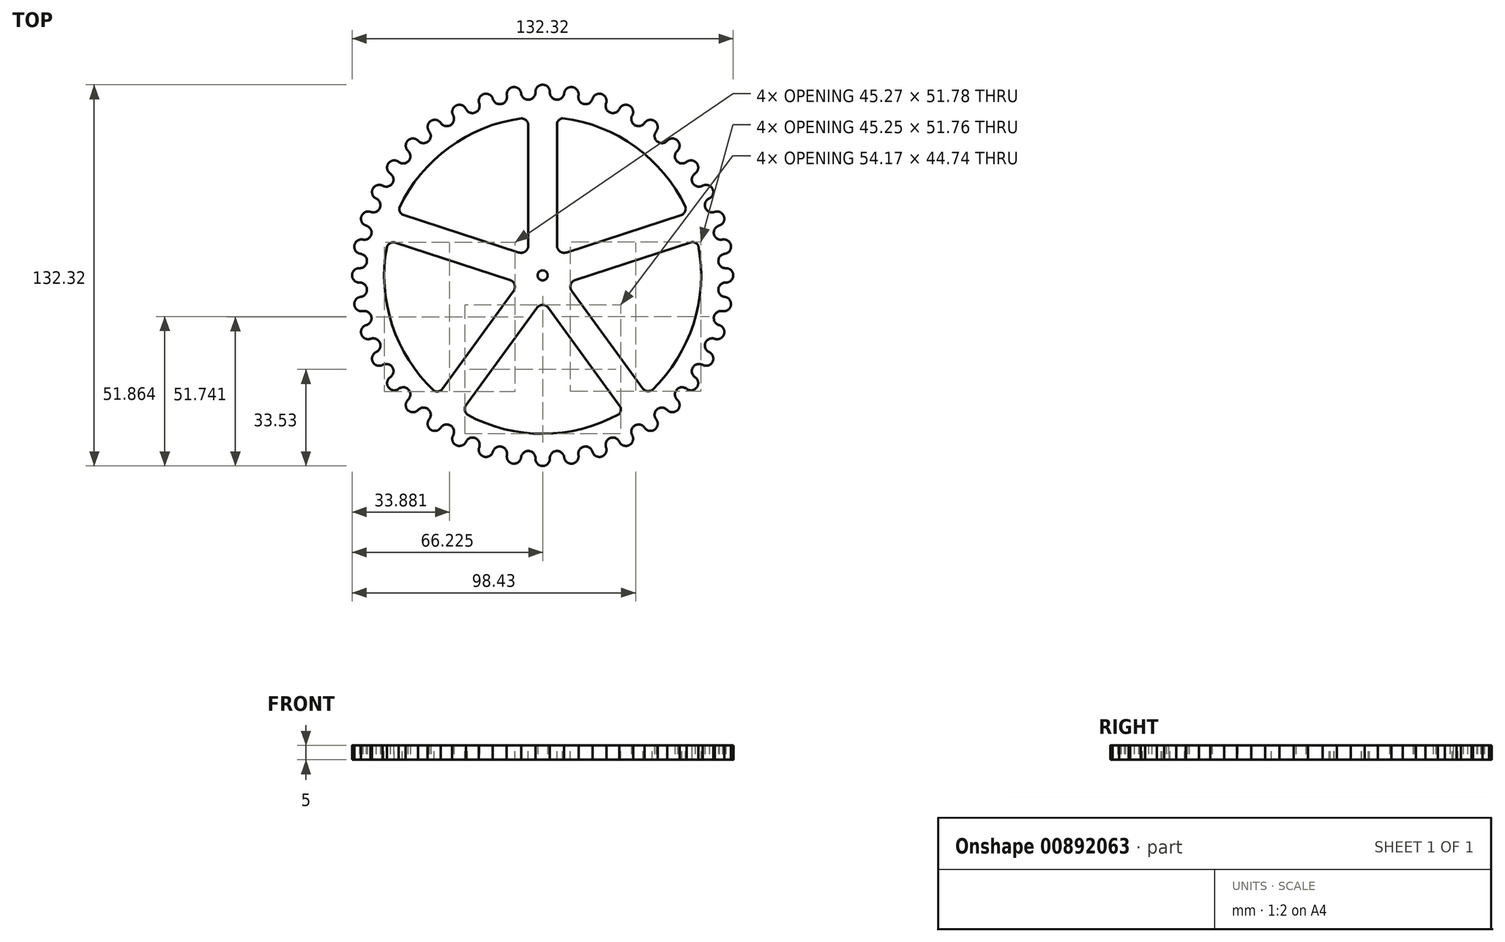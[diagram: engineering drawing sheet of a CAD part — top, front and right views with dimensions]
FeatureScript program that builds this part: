
annotation { "Feature Type Name" : "Feature", "Feature Type Description" : "" }
export const myFeature = defineFeature(function(context is Context, id is Id, definition is map)
    precondition{}
    {
        {
            var Q0;
            Q0=qCreatedBy(makeId("Top.planeOp"),FACE);
            var sketch = newSketch(context, id + "F0", { "sketchPlane" : qUnion([Q0])});
            skCircle(sketch, "E0", {"center": v(0, 0) * mm, "radius": 63.66 * mm});
            skArc(sketch, "E1", {"start": v(2.5, 63.61) * mm, "mid": v(0, 66.16) * mm, "end": v(-2.5, 63.61) * mm});
            skArc(sketch, "E2.1.0", {"start": v(-7.48, 63.22) * mm, "mid": v(-10.35, 65.35) * mm, "end": v(-12.42, 62.44) * mm});
            skArc(sketch, "E2.2.0", {"start": v(-17.28, 61.27) * mm, "mid": v(-20.45, 62.92) * mm, "end": v(-22.03, 59.73) * mm});
            skArc(sketch, "E2.3.0", {"start": v(-26.65, 57.81) * mm, "mid": v(-30.04, 58.95) * mm, "end": v(-31.1, 55.54) * mm});
            skArc(sketch, "E2.4.0", {"start": v(-35.37, 52.93) * mm, "mid": v(-38.89, 53.53) * mm, "end": v(-39.41, 50) * mm});
            skArc(sketch, "E2.5.0", {"start": v(-43.21, 46.75) * mm, "mid": v(-46.78, 46.78) * mm, "end": v(-46.75, 43.21) * mm});
            skArc(sketch, "E2.6.0", {"start": v(-50, 39.41) * mm, "mid": v(-53.53, 38.89) * mm, "end": v(-52.93, 35.37) * mm});
            skArc(sketch, "E2.7.0", {"start": v(-55.54, 31.1) * mm, "mid": v(-58.95, 30.04) * mm, "end": v(-57.81, 26.65) * mm});
            skArc(sketch, "E2.8.0", {"start": v(-59.73, 22.03) * mm, "mid": v(-62.92, 20.45) * mm, "end": v(-61.27, 17.28) * mm});
            skArc(sketch, "E2.9.0", {"start": v(-62.44, 12.42) * mm, "mid": v(-65.35, 10.35) * mm, "end": v(-63.22, 7.48) * mm});
            skArc(sketch, "E2.10.0", {"start": v(-63.61, 2.5) * mm, "mid": v(-66.16, 0) * mm, "end": v(-63.61, -2.5) * mm});
            skArc(sketch, "E2.11.0", {"start": v(-63.22, -7.48) * mm, "mid": v(-65.35, -10.35) * mm, "end": v(-62.44, -12.42) * mm});
            skArc(sketch, "E2.12.0", {"start": v(-61.27, -17.28) * mm, "mid": v(-62.92, -20.45) * mm, "end": v(-59.73, -22.03) * mm});
            skArc(sketch, "E2.13.0", {"start": v(-57.81, -26.65) * mm, "mid": v(-58.95, -30.04) * mm, "end": v(-55.54, -31.1) * mm});
            skArc(sketch, "E2.14.0", {"start": v(-52.93, -35.37) * mm, "mid": v(-53.53, -38.89) * mm, "end": v(-50, -39.41) * mm});
            skArc(sketch, "E2.15.0", {"start": v(-46.75, -43.21) * mm, "mid": v(-46.78, -46.78) * mm, "end": v(-43.21, -46.75) * mm});
            skArc(sketch, "E2.16.0", {"start": v(-39.41, -50) * mm, "mid": v(-38.89, -53.53) * mm, "end": v(-35.37, -52.93) * mm});
            skArc(sketch, "E2.17.0", {"start": v(-31.1, -55.54) * mm, "mid": v(-30.04, -58.95) * mm, "end": v(-26.65, -57.81) * mm});
            skArc(sketch, "E2.18.0", {"start": v(-22.03, -59.73) * mm, "mid": v(-20.45, -62.92) * mm, "end": v(-17.28, -61.27) * mm});
            skArc(sketch, "E2.19.0", {"start": v(-12.42, -62.44) * mm, "mid": v(-10.35, -65.35) * mm, "end": v(-7.48, -63.22) * mm});
            skLineSegment(sketch, "E3", {"start": v(0, 0) * mm, "end": v(6.13, 77.9) * mm});
            skArc(sketch, "E4", {"start": v(2.5, 63.61) * mm, "mid": v(4.8, 60.97) * mm, "end": v(7.48, 63.22) * mm});
            skArc(sketch, "E5.1.0", {"start": v(-7.48, 63.22) * mm, "mid": v(-4.8, 60.97) * mm, "end": v(-2.5, 63.61) * mm});
            skArc(sketch, "E5.2.0", {"start": v(-17.28, 61.27) * mm, "mid": v(-14.28, 59.47) * mm, "end": v(-12.42, 62.44) * mm});
            skArc(sketch, "E5.3.0", {"start": v(-26.65, 57.81) * mm, "mid": v(-23.4, 56.5) * mm, "end": v(-22.03, 59.73) * mm});
            skArc(sketch, "E5.4.0", {"start": v(-35.37, 52.93) * mm, "mid": v(-31.96, 52.15) * mm, "end": v(-31.1, 55.54) * mm});
            skArc(sketch, "E5.5.0", {"start": v(-43.21, 46.75) * mm, "mid": v(-39.72, 46.5) * mm, "end": v(-39.41, 50) * mm});
            skArc(sketch, "E5.6.0", {"start": v(-50, 39.41) * mm, "mid": v(-46.5, 39.72) * mm, "end": v(-46.75, 43.21) * mm});
            skArc(sketch, "E5.7.0", {"start": v(-55.54, 31.1) * mm, "mid": v(-52.15, 31.96) * mm, "end": v(-52.93, 35.37) * mm});
            skArc(sketch, "E5.8.0", {"start": v(-59.73, 22.03) * mm, "mid": v(-56.5, 23.4) * mm, "end": v(-57.81, 26.65) * mm});
            skArc(sketch, "E5.9.0", {"start": v(-62.44, 12.42) * mm, "mid": v(-59.47, 14.28) * mm, "end": v(-61.27, 17.28) * mm});
            skArc(sketch, "E5.10.0", {"start": v(-63.61, 2.5) * mm, "mid": v(-60.97, 4.8) * mm, "end": v(-63.22, 7.48) * mm});
            skArc(sketch, "E5.11.0", {"start": v(-63.22, -7.48) * mm, "mid": v(-60.97, -4.8) * mm, "end": v(-63.61, -2.5) * mm});
            skArc(sketch, "E5.12.0", {"start": v(-61.27, -17.28) * mm, "mid": v(-59.47, -14.28) * mm, "end": v(-62.44, -12.42) * mm});
            skArc(sketch, "E5.13.0", {"start": v(-57.81, -26.65) * mm, "mid": v(-56.5, -23.4) * mm, "end": v(-59.73, -22.03) * mm});
            skArc(sketch, "E5.14.0", {"start": v(-52.93, -35.37) * mm, "mid": v(-52.15, -31.96) * mm, "end": v(-55.54, -31.1) * mm});
            skArc(sketch, "E5.15.0", {"start": v(-46.75, -43.21) * mm, "mid": v(-46.5, -39.72) * mm, "end": v(-50, -39.41) * mm});
            skArc(sketch, "E5.16.0", {"start": v(-39.41, -50) * mm, "mid": v(-39.72, -46.5) * mm, "end": v(-43.21, -46.75) * mm});
            skArc(sketch, "E5.17.0", {"start": v(-31.1, -55.54) * mm, "mid": v(-31.96, -52.15) * mm, "end": v(-35.37, -52.93) * mm});
            skArc(sketch, "E5.18.0", {"start": v(-22.03, -59.73) * mm, "mid": v(-23.4, -56.5) * mm, "end": v(-26.65, -57.81) * mm});
            skArc(sketch, "E5.19.0", {"start": v(-12.42, -62.44) * mm, "mid": v(-14.28, -59.47) * mm, "end": v(-17.28, -61.27) * mm});
            skArc(sketch, "E6.3.20.0", {"start": v(-2.5, -63.61) * mm, "mid": v(0, -66.16) * mm, "end": v(2.5, -63.61) * mm});
            skArc(sketch, "E6.3.21.0", {"start": v(7.48, -63.22) * mm, "mid": v(10.35, -65.35) * mm, "end": v(12.42, -62.44) * mm});
            skArc(sketch, "E6.3.22.0", {"start": v(17.28, -61.27) * mm, "mid": v(20.45, -62.92) * mm, "end": v(22.03, -59.73) * mm});
            skArc(sketch, "E6.3.23.0", {"start": v(26.65, -57.81) * mm, "mid": v(30.04, -58.95) * mm, "end": v(31.1, -55.54) * mm});
            skArc(sketch, "E6.3.24.0", {"start": v(35.37, -52.93) * mm, "mid": v(38.89, -53.53) * mm, "end": v(39.41, -50) * mm});
            skArc(sketch, "E6.3.25.0", {"start": v(43.21, -46.75) * mm, "mid": v(46.78, -46.78) * mm, "end": v(46.75, -43.21) * mm});
            skArc(sketch, "E6.3.26.0", {"start": v(50, -39.41) * mm, "mid": v(53.53, -38.89) * mm, "end": v(52.93, -35.37) * mm});
            skArc(sketch, "E6.3.27.0", {"start": v(55.54, -31.1) * mm, "mid": v(58.95, -30.04) * mm, "end": v(57.81, -26.65) * mm});
            skArc(sketch, "E6.3.28.0", {"start": v(59.73, -22.03) * mm, "mid": v(62.92, -20.45) * mm, "end": v(61.27, -17.28) * mm});
            skArc(sketch, "E6.3.29.0", {"start": v(62.44, -12.42) * mm, "mid": v(65.35, -10.35) * mm, "end": v(63.22, -7.48) * mm});
            skArc(sketch, "E6.3.30.0", {"start": v(63.61, -2.5) * mm, "mid": v(66.16, 0) * mm, "end": v(63.61, 2.5) * mm});
            skArc(sketch, "E6.3.31.0", {"start": v(63.22, 7.48) * mm, "mid": v(65.35, 10.35) * mm, "end": v(62.44, 12.42) * mm});
            skArc(sketch, "E6.3.32.0", {"start": v(61.27, 17.28) * mm, "mid": v(62.92, 20.45) * mm, "end": v(59.73, 22.03) * mm});
            skArc(sketch, "E6.3.33.0", {"start": v(57.81, 26.65) * mm, "mid": v(58.95, 30.04) * mm, "end": v(55.54, 31.1) * mm});
            skArc(sketch, "E6.3.34.0", {"start": v(52.93, 35.37) * mm, "mid": v(53.53, 38.89) * mm, "end": v(50, 39.41) * mm});
            skArc(sketch, "E6.3.35.0", {"start": v(46.75, 43.21) * mm, "mid": v(46.78, 46.78) * mm, "end": v(43.21, 46.75) * mm});
            skArc(sketch, "E6.3.36.0", {"start": v(39.41, 50) * mm, "mid": v(38.89, 53.53) * mm, "end": v(35.37, 52.93) * mm});
            skArc(sketch, "E6.3.37.0", {"start": v(31.1, 55.54) * mm, "mid": v(30.04, 58.95) * mm, "end": v(26.65, 57.81) * mm});
            skArc(sketch, "E6.3.38.0", {"start": v(22.03, 59.73) * mm, "mid": v(20.45, 62.92) * mm, "end": v(17.28, 61.27) * mm});
            skArc(sketch, "E6.3.39.0", {"start": v(12.42, 62.44) * mm, "mid": v(10.35, 65.35) * mm, "end": v(7.48, 63.22) * mm});
            skArc(sketch, "E7.2.20.0", {"start": v(-2.5, -63.61) * mm, "mid": v(-4.8, -60.97) * mm, "end": v(-7.48, -63.22) * mm});
            skArc(sketch, "E7.2.21.0", {"start": v(7.48, -63.22) * mm, "mid": v(4.8, -60.97) * mm, "end": v(2.5, -63.61) * mm});
            skArc(sketch, "E7.2.22.0", {"start": v(17.28, -61.27) * mm, "mid": v(14.28, -59.47) * mm, "end": v(12.42, -62.44) * mm});
            skArc(sketch, "E7.2.23.0", {"start": v(26.65, -57.81) * mm, "mid": v(23.4, -56.5) * mm, "end": v(22.03, -59.73) * mm});
            skArc(sketch, "E7.2.24.0", {"start": v(35.37, -52.93) * mm, "mid": v(31.96, -52.15) * mm, "end": v(31.1, -55.54) * mm});
            skArc(sketch, "E7.2.25.0", {"start": v(43.21, -46.75) * mm, "mid": v(39.72, -46.5) * mm, "end": v(39.41, -50) * mm});
            skArc(sketch, "E7.2.26.0", {"start": v(50, -39.41) * mm, "mid": v(46.5, -39.72) * mm, "end": v(46.75, -43.21) * mm});
            skArc(sketch, "E7.2.27.0", {"start": v(55.54, -31.1) * mm, "mid": v(52.15, -31.96) * mm, "end": v(52.93, -35.37) * mm});
            skArc(sketch, "E7.2.28.0", {"start": v(59.73, -22.03) * mm, "mid": v(56.5, -23.4) * mm, "end": v(57.81, -26.65) * mm});
            skArc(sketch, "E7.2.29.0", {"start": v(62.44, -12.42) * mm, "mid": v(59.47, -14.28) * mm, "end": v(61.27, -17.28) * mm});
            skArc(sketch, "E7.2.30.0", {"start": v(63.61, -2.5) * mm, "mid": v(60.97, -4.8) * mm, "end": v(63.22, -7.48) * mm});
            skArc(sketch, "E7.2.31.0", {"start": v(63.22, 7.48) * mm, "mid": v(60.97, 4.8) * mm, "end": v(63.61, 2.5) * mm});
            skArc(sketch, "E7.2.32.0", {"start": v(61.27, 17.28) * mm, "mid": v(59.47, 14.28) * mm, "end": v(62.44, 12.42) * mm});
            skArc(sketch, "E7.2.33.0", {"start": v(57.81, 26.65) * mm, "mid": v(56.5, 23.4) * mm, "end": v(59.73, 22.03) * mm});
            skArc(sketch, "E7.2.34.0", {"start": v(52.93, 35.37) * mm, "mid": v(52.15, 31.96) * mm, "end": v(55.54, 31.1) * mm});
            skArc(sketch, "E7.2.35.0", {"start": v(46.75, 43.21) * mm, "mid": v(46.5, 39.72) * mm, "end": v(50, 39.41) * mm});
            skArc(sketch, "E7.2.36.0", {"start": v(39.41, 50) * mm, "mid": v(39.72, 46.5) * mm, "end": v(43.21, 46.75) * mm});
            skArc(sketch, "E7.2.37.0", {"start": v(31.1, 55.54) * mm, "mid": v(31.96, 52.15) * mm, "end": v(35.37, 52.93) * mm});
            skArc(sketch, "E7.2.38.0", {"start": v(22.03, 59.73) * mm, "mid": v(23.4, 56.5) * mm, "end": v(26.65, 57.81) * mm});
            skArc(sketch, "E7.2.39.0", {"start": v(12.42, 62.44) * mm, "mid": v(14.28, 59.47) * mm, "end": v(17.28, 61.27) * mm});
            skSolve(sketch);
        }
        {
            var Q0;
            {var subQ22=sQuery(id+"F0.wireOp",EDGE,"E5.1.0");Q0=makeQuery(id+"F0.imprint","IMPRINT",FACE,{"disambiguationData":[TD([[makeQuery(id+"F0.imprint","IMPRINT",EDGE,{"derivedFrom":subQ22}),-1.0]])]});}
            var Q1;
            {var subQ0=sQuery(id+"F0.wireOp",EDGE,"E2.19.0");Q1=makeQuery(id+"F0.imprint","IMPRINT",FACE,{"disambiguationData":[TD([[makeQuery(id+"F0.imprint","IMPRINT",EDGE,{"derivedFrom":subQ0}),1.0]])]});}
            var Q2;
            {var subQ0=sQuery(id+"F0.wireOp",EDGE,"E1");Q2=makeQuery(id+"F0.imprint","IMPRINT",FACE,{"disambiguationData":[TD([[makeQuery(id+"F0.imprint","IMPRINT",EDGE,{"derivedFrom":subQ0}),1.0]])]});}
            var Q3;
            {var subQ0=sQuery(id+"F0.wireOp",EDGE,"E2.1.0");Q3=makeQuery(id+"F0.imprint","IMPRINT",FACE,{"disambiguationData":[TD([[makeQuery(id+"F0.imprint","IMPRINT",EDGE,{"derivedFrom":subQ0}),1.0]])]});}
            var Q4;
            {var subQ0=sQuery(id+"F0.wireOp",EDGE,"E2.2.0");Q4=makeQuery(id+"F0.imprint","IMPRINT",FACE,{"disambiguationData":[TD([[makeQuery(id+"F0.imprint","IMPRINT",EDGE,{"derivedFrom":subQ0}),1.0]])]});}
            var Q5;
            {var subQ0=sQuery(id+"F0.wireOp",EDGE,"E2.3.0");Q5=makeQuery(id+"F0.imprint","IMPRINT",FACE,{"disambiguationData":[TD([[makeQuery(id+"F0.imprint","IMPRINT",EDGE,{"derivedFrom":subQ0}),1.0]])]});}
            var Q6;
            {var subQ0=sQuery(id+"F0.wireOp",EDGE,"E2.4.0");Q6=makeQuery(id+"F0.imprint","IMPRINT",FACE,{"disambiguationData":[TD([[makeQuery(id+"F0.imprint","IMPRINT",EDGE,{"derivedFrom":subQ0}),1.0]])]});}
            var Q7;
            {var subQ0=sQuery(id+"F0.wireOp",EDGE,"E2.5.0");Q7=makeQuery(id+"F0.imprint","IMPRINT",FACE,{"disambiguationData":[TD([[makeQuery(id+"F0.imprint","IMPRINT",EDGE,{"derivedFrom":subQ0}),1.0]])]});}
            var Q8;
            {var subQ0=sQuery(id+"F0.wireOp",EDGE,"E2.6.0");Q8=makeQuery(id+"F0.imprint","IMPRINT",FACE,{"disambiguationData":[TD([[makeQuery(id+"F0.imprint","IMPRINT",EDGE,{"derivedFrom":subQ0}),1.0]])]});}
            var Q9;
            {var subQ0=sQuery(id+"F0.wireOp",EDGE,"E2.7.0");Q9=makeQuery(id+"F0.imprint","IMPRINT",FACE,{"disambiguationData":[TD([[makeQuery(id+"F0.imprint","IMPRINT",EDGE,{"derivedFrom":subQ0}),1.0]])]});}
            var Q10;
            {var subQ0=sQuery(id+"F0.wireOp",EDGE,"E2.8.0");Q10=makeQuery(id+"F0.imprint","IMPRINT",FACE,{"disambiguationData":[TD([[makeQuery(id+"F0.imprint","IMPRINT",EDGE,{"derivedFrom":subQ0}),1.0]])]});}
            var Q11;
            {var subQ0=sQuery(id+"F0.wireOp",EDGE,"E2.9.0");Q11=makeQuery(id+"F0.imprint","IMPRINT",FACE,{"disambiguationData":[TD([[makeQuery(id+"F0.imprint","IMPRINT",EDGE,{"derivedFrom":subQ0}),1.0]])]});}
            var Q12;
            {var subQ0=sQuery(id+"F0.wireOp",EDGE,"E2.10.0");Q12=makeQuery(id+"F0.imprint","IMPRINT",FACE,{"disambiguationData":[TD([[makeQuery(id+"F0.imprint","IMPRINT",EDGE,{"derivedFrom":subQ0}),1.0]])]});}
            var Q13;
            {var subQ0=sQuery(id+"F0.wireOp",EDGE,"E2.11.0");Q13=makeQuery(id+"F0.imprint","IMPRINT",FACE,{"disambiguationData":[TD([[makeQuery(id+"F0.imprint","IMPRINT",EDGE,{"derivedFrom":subQ0}),1.0]])]});}
            var Q14;
            {var subQ0=sQuery(id+"F0.wireOp",EDGE,"E2.12.0");Q14=makeQuery(id+"F0.imprint","IMPRINT",FACE,{"disambiguationData":[TD([[makeQuery(id+"F0.imprint","IMPRINT",EDGE,{"derivedFrom":subQ0}),1.0]])]});}
            var Q15;
            {var subQ0=sQuery(id+"F0.wireOp",EDGE,"E2.13.0");Q15=makeQuery(id+"F0.imprint","IMPRINT",FACE,{"disambiguationData":[TD([[makeQuery(id+"F0.imprint","IMPRINT",EDGE,{"derivedFrom":subQ0}),1.0]])]});}
            var Q16;
            {var subQ0=sQuery(id+"F0.wireOp",EDGE,"E2.14.0");Q16=makeQuery(id+"F0.imprint","IMPRINT",FACE,{"disambiguationData":[TD([[makeQuery(id+"F0.imprint","IMPRINT",EDGE,{"derivedFrom":subQ0}),1.0]])]});}
            var Q17;
            {var subQ0=sQuery(id+"F0.wireOp",EDGE,"E2.15.0");Q17=makeQuery(id+"F0.imprint","IMPRINT",FACE,{"disambiguationData":[TD([[makeQuery(id+"F0.imprint","IMPRINT",EDGE,{"derivedFrom":subQ0}),1.0]])]});}
            var Q18;
            {var subQ0=sQuery(id+"F0.wireOp",EDGE,"E2.16.0");Q18=makeQuery(id+"F0.imprint","IMPRINT",FACE,{"disambiguationData":[TD([[makeQuery(id+"F0.imprint","IMPRINT",EDGE,{"derivedFrom":subQ0}),1.0]])]});}
            var Q19;
            {var subQ0=sQuery(id+"F0.wireOp",EDGE,"E2.17.0");Q19=makeQuery(id+"F0.imprint","IMPRINT",FACE,{"disambiguationData":[TD([[makeQuery(id+"F0.imprint","IMPRINT",EDGE,{"derivedFrom":subQ0}),1.0]])]});}
            var Q20;
            {var subQ0=sQuery(id+"F0.wireOp",EDGE,"E2.18.0");Q20=makeQuery(id+"F0.imprint","IMPRINT",FACE,{"disambiguationData":[TD([[makeQuery(id+"F0.imprint","IMPRINT",EDGE,{"derivedFrom":subQ0}),1.0]])]});}
            var Q21;
            {var subQ0=sQuery(id+"F0.wireOp",EDGE,"E6.3.20.0");Q21=makeQuery(id+"F0.imprint","IMPRINT",FACE,{"disambiguationData":[TD([[makeQuery(id+"F0.imprint","IMPRINT",EDGE,{"derivedFrom":subQ0}),1.0]])]});}
            var Q22;
            {var subQ0=sQuery(id+"F0.wireOp",EDGE,"E6.3.21.0");Q22=makeQuery(id+"F0.imprint","IMPRINT",FACE,{"disambiguationData":[TD([[makeQuery(id+"F0.imprint","IMPRINT",EDGE,{"derivedFrom":subQ0}),1.0]])]});}
            var Q23;
            {var subQ0=sQuery(id+"F0.wireOp",EDGE,"E6.3.22.0");Q23=makeQuery(id+"F0.imprint","IMPRINT",FACE,{"disambiguationData":[TD([[makeQuery(id+"F0.imprint","IMPRINT",EDGE,{"derivedFrom":subQ0}),1.0]])]});}
            var Q24;
            {var subQ0=sQuery(id+"F0.wireOp",EDGE,"E6.3.23.0");Q24=makeQuery(id+"F0.imprint","IMPRINT",FACE,{"disambiguationData":[TD([[makeQuery(id+"F0.imprint","IMPRINT",EDGE,{"derivedFrom":subQ0}),1.0]])]});}
            var Q25;
            {var subQ0=sQuery(id+"F0.wireOp",EDGE,"E6.3.24.0");Q25=makeQuery(id+"F0.imprint","IMPRINT",FACE,{"disambiguationData":[TD([[makeQuery(id+"F0.imprint","IMPRINT",EDGE,{"derivedFrom":subQ0}),1.0]])]});}
            var Q26;
            {var subQ0=sQuery(id+"F0.wireOp",EDGE,"E6.3.26.0");Q26=makeQuery(id+"F0.imprint","IMPRINT",FACE,{"disambiguationData":[TD([[makeQuery(id+"F0.imprint","IMPRINT",EDGE,{"derivedFrom":subQ0}),1.0]])]});}
            var Q27;
            {var subQ0=sQuery(id+"F0.wireOp",EDGE,"E6.3.27.0");Q27=makeQuery(id+"F0.imprint","IMPRINT",FACE,{"disambiguationData":[TD([[makeQuery(id+"F0.imprint","IMPRINT",EDGE,{"derivedFrom":subQ0}),1.0]])]});}
            var Q28;
            {var subQ0=sQuery(id+"F0.wireOp",EDGE,"E6.3.28.0");Q28=makeQuery(id+"F0.imprint","IMPRINT",FACE,{"disambiguationData":[TD([[makeQuery(id+"F0.imprint","IMPRINT",EDGE,{"derivedFrom":subQ0}),1.0]])]});}
            var Q29;
            {var subQ0=sQuery(id+"F0.wireOp",EDGE,"E6.3.29.0");Q29=makeQuery(id+"F0.imprint","IMPRINT",FACE,{"disambiguationData":[TD([[makeQuery(id+"F0.imprint","IMPRINT",EDGE,{"derivedFrom":subQ0}),1.0]])]});}
            var Q30;
            {var subQ0=sQuery(id+"F0.wireOp",EDGE,"E6.3.30.0");Q30=makeQuery(id+"F0.imprint","IMPRINT",FACE,{"disambiguationData":[TD([[makeQuery(id+"F0.imprint","IMPRINT",EDGE,{"derivedFrom":subQ0}),1.0]])]});}
            var Q31;
            {var subQ0=sQuery(id+"F0.wireOp",EDGE,"E6.3.31.0");Q31=makeQuery(id+"F0.imprint","IMPRINT",FACE,{"disambiguationData":[TD([[makeQuery(id+"F0.imprint","IMPRINT",EDGE,{"derivedFrom":subQ0}),1.0]])]});}
            var Q32;
            {var subQ0=sQuery(id+"F0.wireOp",EDGE,"E6.3.32.0");Q32=makeQuery(id+"F0.imprint","IMPRINT",FACE,{"disambiguationData":[TD([[makeQuery(id+"F0.imprint","IMPRINT",EDGE,{"derivedFrom":subQ0}),1.0]])]});}
            var Q33;
            {var subQ0=sQuery(id+"F0.wireOp",EDGE,"E6.3.33.0");Q33=makeQuery(id+"F0.imprint","IMPRINT",FACE,{"disambiguationData":[TD([[makeQuery(id+"F0.imprint","IMPRINT",EDGE,{"derivedFrom":subQ0}),1.0]])]});}
            var Q34;
            {var subQ0=sQuery(id+"F0.wireOp",EDGE,"E6.3.34.0");Q34=makeQuery(id+"F0.imprint","IMPRINT",FACE,{"disambiguationData":[TD([[makeQuery(id+"F0.imprint","IMPRINT",EDGE,{"derivedFrom":subQ0}),1.0]])]});}
            var Q35;
            {var subQ0=sQuery(id+"F0.wireOp",EDGE,"E6.3.35.0");Q35=makeQuery(id+"F0.imprint","IMPRINT",FACE,{"disambiguationData":[TD([[makeQuery(id+"F0.imprint","IMPRINT",EDGE,{"derivedFrom":subQ0}),1.0]])]});}
            var Q36;
            {var subQ0=sQuery(id+"F0.wireOp",EDGE,"E6.3.39.0");Q36=makeQuery(id+"F0.imprint","IMPRINT",FACE,{"disambiguationData":[TD([[makeQuery(id+"F0.imprint","IMPRINT",EDGE,{"derivedFrom":subQ0}),1.0]])]});}
            var Q37;
            {var subQ0=sQuery(id+"F0.wireOp",EDGE,"E6.3.38.0");Q37=makeQuery(id+"F0.imprint","IMPRINT",FACE,{"disambiguationData":[TD([[makeQuery(id+"F0.imprint","IMPRINT",EDGE,{"derivedFrom":subQ0}),1.0]])]});}
            var Q38;
            {var subQ0=sQuery(id+"F0.wireOp",EDGE,"E6.3.37.0");Q38=makeQuery(id+"F0.imprint","IMPRINT",FACE,{"disambiguationData":[TD([[makeQuery(id+"F0.imprint","IMPRINT",EDGE,{"derivedFrom":subQ0}),1.0]])]});}
            var Q39;
            {var subQ0=sQuery(id+"F0.wireOp",EDGE,"E6.3.36.0");Q39=makeQuery(id+"F0.imprint","IMPRINT",FACE,{"disambiguationData":[TD([[makeQuery(id+"F0.imprint","IMPRINT",EDGE,{"derivedFrom":subQ0}),1.0]])]});}
            var Q40;
            {var subQ0=sQuery(id+"F0.wireOp",EDGE,"E6.3.25.0");Q40=makeQuery(id+"F0.imprint","IMPRINT",FACE,{"disambiguationData":[TD([[makeQuery(id+"F0.imprint","IMPRINT",EDGE,{"derivedFrom":subQ0}),1.0]])]});}
            extrude(context, id + "F1", {"entities" : qUnion([Q0, Q1, Q2, Q3, Q4, Q5, Q6, Q7, Q8, Q9, Q10, Q11, Q12, Q13, Q14, Q15, Q16, Q17, Q18, Q19, Q20, Q21, Q22, Q23, Q24, Q25, Q26, Q27, Q28, Q29, Q30, Q31, Q32, Q33, Q34, Q35, Q36, Q37, Q38, Q39, Q40]), "depth" : 5 * mm, "offsetDistance" : 25 * mm});
        }
        {
            var Q0;
            Q0=sQuery(id+"F0.wireOp",VERTEX,"E0.center");
            var Q1;
            Q1=makeQuery(id+"F1.opExtrude","SWEPT_BODY",BODY,{"disambiguationData":[OSD([sQuery(id+"F0.wireOp",EDGE,"E0"),sQuery(id+"F0.wireOp",EDGE,"E1"),sQuery(id+"F0.wireOp",EDGE,"E2.1.0"),sQuery(id+"F0.wireOp",EDGE,"E2.2.0"),sQuery(id+"F0.wireOp",EDGE,"E2.3.0"),sQuery(id+"F0.wireOp",EDGE,"E2.4.0"),sQuery(id+"F0.wireOp",EDGE,"E2.5.0"),sQuery(id+"F0.wireOp",EDGE,"E2.6.0"),sQuery(id+"F0.wireOp",EDGE,"E2.7.0"),sQuery(id+"F0.wireOp",EDGE,"E2.8.0"),sQuery(id+"F0.wireOp",EDGE,"E2.9.0"),sQuery(id+"F0.wireOp",EDGE,"E2.10.0"),sQuery(id+"F0.wireOp",EDGE,"E2.11.0"),sQuery(id+"F0.wireOp",EDGE,"E2.12.0"),sQuery(id+"F0.wireOp",EDGE,"E2.13.0"),sQuery(id+"F0.wireOp",EDGE,"E2.14.0"),sQuery(id+"F0.wireOp",EDGE,"E2.15.0"),sQuery(id+"F0.wireOp",EDGE,"E2.16.0"),sQuery(id+"F0.wireOp",EDGE,"E2.17.0"),sQuery(id+"F0.wireOp",EDGE,"E2.18.0"),sQuery(id+"F0.wireOp",EDGE,"E2.19.0"),sQuery(id+"F0.wireOp",EDGE,"E4"),sQuery(id+"F0.wireOp",EDGE,"E5.1.0"),sQuery(id+"F0.wireOp",EDGE,"E5.2.0"),sQuery(id+"F0.wireOp",EDGE,"E5.3.0"),sQuery(id+"F0.wireOp",EDGE,"E5.4.0"),sQuery(id+"F0.wireOp",EDGE,"E5.5.0"),sQuery(id+"F0.wireOp",EDGE,"E5.6.0"),sQuery(id+"F0.wireOp",EDGE,"E5.7.0"),sQuery(id+"F0.wireOp",EDGE,"E5.8.0"),sQuery(id+"F0.wireOp",EDGE,"E5.9.0"),sQuery(id+"F0.wireOp",EDGE,"E5.10.0"),sQuery(id+"F0.wireOp",EDGE,"E5.11.0"),sQuery(id+"F0.wireOp",EDGE,"E5.12.0"),sQuery(id+"F0.wireOp",EDGE,"E5.13.0"),sQuery(id+"F0.wireOp",EDGE,"E5.14.0"),sQuery(id+"F0.wireOp",EDGE,"E5.15.0"),sQuery(id+"F0.wireOp",EDGE,"E5.16.0"),sQuery(id+"F0.wireOp",EDGE,"E5.17.0"),sQuery(id+"F0.wireOp",EDGE,"E5.18.0"),sQuery(id+"F0.wireOp",EDGE,"E5.19.0")])]});
            hole(context, id + "F2", {"style" : HoleStyle.SIMPLE, "endStyle" : HoleEndStyle.THROUGH, "oppositeDirection" : true, "holeDiameter" : 3.5 * mm, "majorDiameter" : 5 * mm, "isTappedThrough" : true, "tappedDepth" : 12 * mm, "tapClearance" : 3, "locations" : qUnion([Q0]), "scope" : qUnion([Q1])});
        }
        {
            var Q0;
            Q0=makeQuery(id+"F1.opExtrude","CAP_FACE",FACE,{"disambiguationData":[OSD([sQuery(id+"F0.wireOp",EDGE,"E0"),sQuery(id+"F0.wireOp",EDGE,"E1"),sQuery(id+"F0.wireOp",EDGE,"E2.1.0"),sQuery(id+"F0.wireOp",EDGE,"E2.2.0"),sQuery(id+"F0.wireOp",EDGE,"E2.3.0"),sQuery(id+"F0.wireOp",EDGE,"E2.4.0"),sQuery(id+"F0.wireOp",EDGE,"E2.5.0"),sQuery(id+"F0.wireOp",EDGE,"E2.6.0"),sQuery(id+"F0.wireOp",EDGE,"E2.7.0"),sQuery(id+"F0.wireOp",EDGE,"E2.8.0"),sQuery(id+"F0.wireOp",EDGE,"E2.9.0"),sQuery(id+"F0.wireOp",EDGE,"E2.10.0"),sQuery(id+"F0.wireOp",EDGE,"E2.11.0"),sQuery(id+"F0.wireOp",EDGE,"E2.12.0"),sQuery(id+"F0.wireOp",EDGE,"E2.13.0"),sQuery(id+"F0.wireOp",EDGE,"E2.14.0"),sQuery(id+"F0.wireOp",EDGE,"E2.15.0"),sQuery(id+"F0.wireOp",EDGE,"E2.16.0"),sQuery(id+"F0.wireOp",EDGE,"E2.17.0"),sQuery(id+"F0.wireOp",EDGE,"E2.18.0"),sQuery(id+"F0.wireOp",EDGE,"E2.19.0"),sQuery(id+"F0.wireOp",EDGE,"E4"),sQuery(id+"F0.wireOp",EDGE,"E5.1.0"),sQuery(id+"F0.wireOp",EDGE,"E5.2.0"),sQuery(id+"F0.wireOp",EDGE,"E5.3.0"),sQuery(id+"F0.wireOp",EDGE,"E5.4.0"),sQuery(id+"F0.wireOp",EDGE,"E5.5.0"),sQuery(id+"F0.wireOp",EDGE,"E5.6.0"),sQuery(id+"F0.wireOp",EDGE,"E5.7.0"),sQuery(id+"F0.wireOp",EDGE,"E5.8.0"),sQuery(id+"F0.wireOp",EDGE,"E5.9.0"),sQuery(id+"F0.wireOp",EDGE,"E5.10.0"),sQuery(id+"F0.wireOp",EDGE,"E5.11.0"),sQuery(id+"F0.wireOp",EDGE,"E5.12.0"),sQuery(id+"F0.wireOp",EDGE,"E5.13.0"),sQuery(id+"F0.wireOp",EDGE,"E5.14.0"),sQuery(id+"F0.wireOp",EDGE,"E5.15.0"),sQuery(id+"F0.wireOp",EDGE,"E5.16.0"),sQuery(id+"F0.wireOp",EDGE,"E5.17.0"),sQuery(id+"F0.wireOp",EDGE,"E5.18.0"),sQuery(id+"F0.wireOp",EDGE,"E5.19.0"),sQuery(id+"F0.wireOp",EDGE,"E6.3.20.0"),sQuery(id+"F0.wireOp",EDGE,"E6.3.21.0"),sQuery(id+"F0.wireOp",EDGE,"E6.3.22.0"),sQuery(id+"F0.wireOp",EDGE,"E6.3.23.0"),sQuery(id+"F0.wireOp",EDGE,"E6.3.24.0"),sQuery(id+"F0.wireOp",EDGE,"E6.3.25.0"),sQuery(id+"F0.wireOp",EDGE,"E6.3.26.0"),sQuery(id+"F0.wireOp",EDGE,"E6.3.27.0"),sQuery(id+"F0.wireOp",EDGE,"E6.3.28.0"),sQuery(id+"F0.wireOp",EDGE,"E6.3.29.0"),sQuery(id+"F0.wireOp",EDGE,"E6.3.30.0"),sQuery(id+"F0.wireOp",EDGE,"E6.3.31.0"),sQuery(id+"F0.wireOp",EDGE,"E6.3.32.0"),sQuery(id+"F0.wireOp",EDGE,"E6.3.33.0"),sQuery(id+"F0.wireOp",EDGE,"E6.3.34.0"),sQuery(id+"F0.wireOp",EDGE,"E6.3.35.0"),sQuery(id+"F0.wireOp",EDGE,"E6.3.36.0"),sQuery(id+"F0.wireOp",EDGE,"E6.3.37.0"),sQuery(id+"F0.wireOp",EDGE,"E6.3.38.0"),sQuery(id+"F0.wireOp",EDGE,"E6.3.39.0"),sQuery(id+"F0.wireOp",EDGE,"E7.2.20.0"),sQuery(id+"F0.wireOp",EDGE,"E7.2.21.0"),sQuery(id+"F0.wireOp",EDGE,"E7.2.22.0"),sQuery(id+"F0.wireOp",EDGE,"E7.2.23.0"),sQuery(id+"F0.wireOp",EDGE,"E7.2.24.0"),sQuery(id+"F0.wireOp",EDGE,"E7.2.25.0"),sQuery(id+"F0.wireOp",EDGE,"E7.2.26.0"),sQuery(id+"F0.wireOp",EDGE,"E7.2.27.0"),sQuery(id+"F0.wireOp",EDGE,"E7.2.28.0"),sQuery(id+"F0.wireOp",EDGE,"E7.2.29.0"),sQuery(id+"F0.wireOp",EDGE,"E7.2.30.0"),sQuery(id+"F0.wireOp",EDGE,"E7.2.31.0"),sQuery(id+"F0.wireOp",EDGE,"E7.2.32.0"),sQuery(id+"F0.wireOp",EDGE,"E7.2.33.0"),sQuery(id+"F0.wireOp",EDGE,"E7.2.34.0"),sQuery(id+"F0.wireOp",EDGE,"E7.2.35.0"),sQuery(id+"F0.wireOp",EDGE,"E7.2.36.0"),sQuery(id+"F0.wireOp",EDGE,"E7.2.37.0"),sQuery(id+"F0.wireOp",EDGE,"E7.2.38.0"),sQuery(id+"F0.wireOp",EDGE,"E7.2.39.0")])],"isStart":false});
            var sketch = newSketch(context, id + "F3", { "sketchPlane" : qUnion([Q0])});
            skCircle(sketch, "E8", {"center": v(0, 0) * mm, "radius": 7.5 * mm});
            skCircle(sketch, "E9", {"center": v(0, 0) * mm, "radius": 57.5 * mm});
            skLineSegment(sketch, "E10", {"start": v(0, 0) * mm, "end": v(0, 57.5) * mm});
            skLineSegment(sketch, "E11.1.0", {"start": v(0, 0) * mm, "end": v(-54.69, 17.77) * mm});
            skLineSegment(sketch, "E11.2.0", {"start": v(0, 0) * mm, "end": v(-33.8, -46.52) * mm});
            skLineSegment(sketch, "E11.3.0", {"start": v(0, 0) * mm, "end": v(33.8, -46.52) * mm});
            skLineSegment(sketch, "E11.4.0", {"start": v(0, 0) * mm, "end": v(54.69, 17.77) * mm});
            skCircle(sketch, "E12", {"center": v(0, 0) * mm, "radius": 55 * mm});
            skLineSegment(sketch, "E13", {"start": v(-50.55, 21.68) * mm, "end": v(-8.27, 7.95) * mm});
            skLineSegment(sketch, "E14", {"start": v(-5, 54.77) * mm, "end": v(-5, 10.32) * mm});
            skArc(sketch, "E15.filletArc", {"start": v(-8.27, 7.95) * mm, "mid": v(-6.03, 8.3) * mm, "end": v(-5, 10.32) * mm});
            skPoint(sketch, "E16", {"position": v(-47.27, 23.12) * mm});
            skArc(sketch, "E17", {"start": v(-47.27, 20.62) * mm, "mid": v(-49.57, 22.15) * mm, "end": v(-49.06, 24.86) * mm});
            skPoint(sketch, "E18", {"position": v(-7.5, 51.96) * mm});
            skArc(sketch, "E19", {"start": v(-5, 51.45) * mm, "mid": v(-5.83, 53.9) * mm, "end": v(-8.38, 54.36) * mm});
            skArc(sketch, "E20.1.0", {"start": v(-50.47, 11.14) * mm, "mid": v(-53.06, 11.1) * mm, "end": v(-54.29, 8.83) * mm});
            skArc(sketch, "E20.1.1", {"start": v(-34.21, -38.59) * mm, "mid": v(-36.38, -40.3) * mm, "end": v(-38.8, -38.98) * mm});
            skLineSegment(sketch, "E20.1.2", {"start": v(-36.24, -41.37) * mm, "end": v(-10.11, -5.41) * mm});
            skLineSegment(sketch, "E20.1.3", {"start": v(-53.64, 12.17) * mm, "end": v(-11.36, -1.57) * mm});
            skArc(sketch, "E20.1.4", {"start": v(-10.11, -5.41) * mm, "mid": v(-9.76, -3.17) * mm, "end": v(-11.36, -1.57) * mm});
            skArc(sketch, "E20.2.0", {"start": v(-26.2, -44.56) * mm, "mid": v(-26.96, -47.03) * mm, "end": v(-25.17, -48.9) * mm});
            skArc(sketch, "E20.2.1", {"start": v(26.12, -44.46) * mm, "mid": v(27.09, -47.05) * mm, "end": v(25.08, -48.95) * mm});
            skLineSegment(sketch, "E20.2.2", {"start": v(28.15, -47.25) * mm, "end": v(2.02, -11.3) * mm});
            skLineSegment(sketch, "E20.2.3", {"start": v(-28.15, -47.25) * mm, "end": v(-2.02, -11.3) * mm});
            skArc(sketch, "E20.2.4", {"start": v(2.02, -11.3) * mm, "mid": v(0, -10.26) * mm, "end": v(-2.02, -11.3) * mm});
            skArc(sketch, "E20.3.0", {"start": v(34.28, -38.68) * mm, "mid": v(36.4, -40.17) * mm, "end": v(38.73, -39.05) * mm});
            skArc(sketch, "E20.3.1", {"start": v(50.36, 11.1) * mm, "mid": v(53.12, 11.22) * mm, "end": v(54.3, 8.72) * mm});
            skLineSegment(sketch, "E20.3.2", {"start": v(53.64, 12.17) * mm, "end": v(11.36, -1.57) * mm});
            skLineSegment(sketch, "E20.3.3", {"start": v(36.24, -41.37) * mm, "end": v(10.11, -5.41) * mm});
            skArc(sketch, "E20.3.4", {"start": v(11.36, -1.57) * mm, "mid": v(9.76, -3.17) * mm, "end": v(10.11, -5.41) * mm});
            skArc(sketch, "E20.4.0", {"start": v(47.38, 20.65) * mm, "mid": v(49.45, 22.2) * mm, "end": v(49.1, 24.77) * mm});
            skArc(sketch, "E20.4.1", {"start": v(5, 51.33) * mm, "mid": v(5.74, 54) * mm, "end": v(8.48, 54.34) * mm});
            skLineSegment(sketch, "E20.4.2", {"start": v(5, 54.77) * mm, "end": v(5, 10.32) * mm});
            skLineSegment(sketch, "E20.4.3", {"start": v(50.55, 21.68) * mm, "end": v(8.27, 7.95) * mm});
            skArc(sketch, "E20.4.4", {"start": v(5, 10.32) * mm, "mid": v(6.03, 8.3) * mm, "end": v(8.27, 7.95) * mm});
            skSolve(sketch);
        }
        {
            var Q0;
            {var subQ12=sQuery(id+"F3.wireOp",EDGE,"E15.filletArc");Q0=makeQuery(id+"F3.imprint","IMPRINT",FACE,{"disambiguationData":[TD([[makeQuery(id+"F3.imprint","IMPRINT",EDGE,{"derivedFrom":subQ12}),1.0]])]});}
            var Q1;
            {var subQ5=sQuery(id+"F3.wireOp",EDGE,"E20.4.4");Q1=makeQuery(id+"F3.imprint","IMPRINT",FACE,{"disambiguationData":[TD([[makeQuery(id+"F3.imprint","IMPRINT",EDGE,{"derivedFrom":subQ5}),1.0]])]});}
            var Q2;
            {var subQ9=sQuery(id+"F3.wireOp",EDGE,"E20.1.4");Q2=makeQuery(id+"F3.imprint","IMPRINT",FACE,{"disambiguationData":[TD([[makeQuery(id+"F3.imprint","IMPRINT",EDGE,{"derivedFrom":subQ9}),1.0]])]});}
            var Q3;
            {var subQ7=sQuery(id+"F3.wireOp",EDGE,"E20.2.4");Q3=makeQuery(id+"F3.imprint","IMPRINT",FACE,{"disambiguationData":[TD([[makeQuery(id+"F3.imprint","IMPRINT",EDGE,{"derivedFrom":subQ7}),1.0]])]});}
            var Q4;
            {var subQ11=sQuery(id+"F3.wireOp",EDGE,"E20.3.4");Q4=makeQuery(id+"F3.imprint","IMPRINT",FACE,{"disambiguationData":[TD([[makeQuery(id+"F3.imprint","IMPRINT",EDGE,{"derivedFrom":subQ11}),1.0]])]});}
            extrude(context, id + "F4", {"entities" : qUnion([Q0, Q1, Q2, Q3, Q4]), "operationType" : NewBodyOperationType.REMOVE, "oppositeDirection" : true, "depth" : 25 * mm, "offsetDistance" : 25 * mm});
        }
    });
